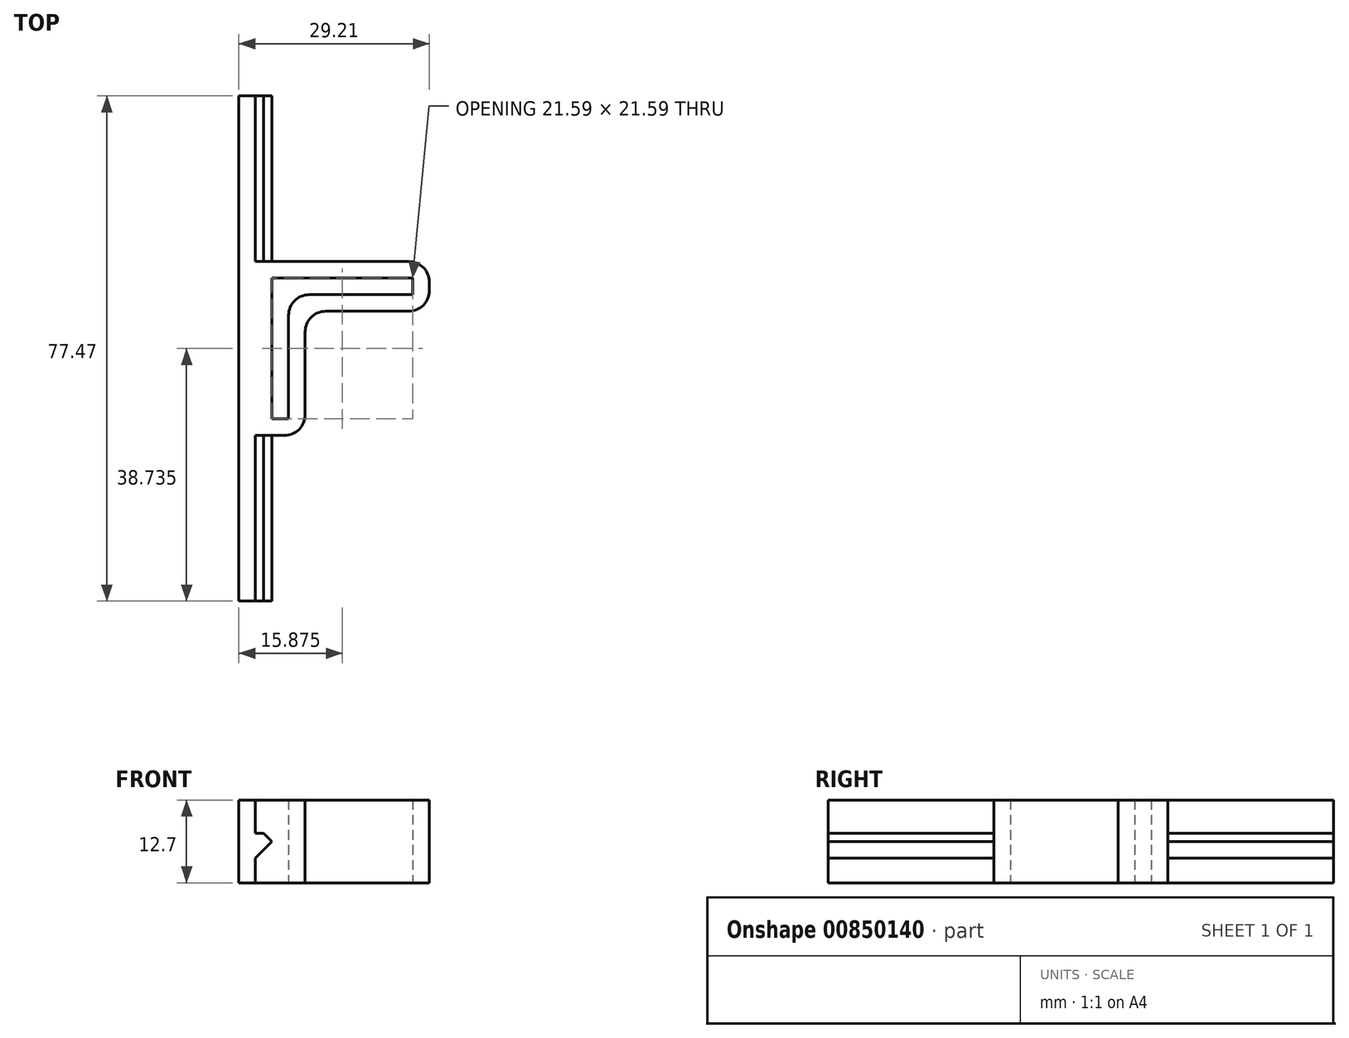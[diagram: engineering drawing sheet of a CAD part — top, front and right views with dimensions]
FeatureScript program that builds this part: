
annotation { "Feature Type Name" : "Feature", "Feature Type Description" : "" }
export const myFeature = defineFeature(function(context is Context, id is Id, definition is map)
    precondition{}
    {
        {
            var Q0;
            Q0=qCreatedBy(makeId("Top.planeOp"),FACE);
            var sketch = newSketch(context, id + "F0", { "sketchPlane" : qUnion([Q0])});
            skLineSegment(sketch, "E0.bottom", {"start": v(2.54, 0) * mm, "end": v(5.08, 0) * mm});
            skLineSegment(sketch, "E0.top", {"start": v(2.54, 21.6) * mm, "end": v(5.08, 21.6) * mm});
            skLineSegment(sketch, "E0.left", {"start": v(2.54, 0) * mm, "end": v(2.54, 21.59) * mm});
            skLineSegment(sketch, "E0.right", {"start": v(5.08, 0) * mm, "end": v(5.08, 19.05) * mm});
            skLineSegment(sketch, "E1.bottom", {"start": v(5.08, 21.6) * mm, "end": v(24.13, 21.6) * mm});
            skLineSegment(sketch, "E1.top", {"start": v(5.08, 19.05) * mm, "end": v(24.13, 19.05) * mm});
            skLineSegment(sketch, "E1.right", {"start": v(24.13, 21.6) * mm, "end": v(24.13, 19.05) * mm});
            skLineSegment(sketch, "E2", {"start": v(0, -2.2) * mm, "end": v(0, 24.13) * mm});
            skLineSegment(sketch, "E3", {"start": v(0, 24.13) * mm, "end": v(26.67, 24.13) * mm});
            skLineSegment(sketch, "E4", {"start": v(26.67, 24.13) * mm, "end": v(26.67, 16.51) * mm});
            skLineSegment(sketch, "E5", {"start": v(26.67, 16.51) * mm, "end": v(7.62, 16.5) * mm});
            skLineSegment(sketch, "E6", {"start": v(7.62, 16.5) * mm, "end": v(7.62, -2.54) * mm});
            skLineSegment(sketch, "E7", {"start": v(7.62, -2.54) * mm, "end": v(0, -2.54) * mm});
            skLineSegment(sketch, "E8", {"start": v(0, -2.54) * mm, "end": v(0, -2.2) * mm});
            skSolve(sketch);
        }
        {
            var Q0;
            Q0=qSketchRegion(id+"F0",true);
            extrude(context, id + "F1", {"entities" : qUnion([Q0]), "depth" : 12.7 * mm, "offsetDistance" : 25.4 * mm});
        }
        {
            var Q0;
            Q0=makeQuery(id+"F1.opExtrude","SWEPT_EDGE",EDGE,{"disambiguationData":[OSD([sQuery(id+"F0.wireOp",EDGE,"E3"),sQuery(id+"F0.wireOp",EDGE,"E4")])]});
            var Q1;
            Q1=makeQuery(id+"F1.opExtrude","SWEPT_EDGE",EDGE,{"disambiguationData":[OSD([sQuery(id+"F0.wireOp",EDGE,"E4"),sQuery(id+"F0.wireOp",EDGE,"E5")])]});
            var Q2;
            Q2=makeQuery(id+"F1.opExtrude","SWEPT_EDGE",EDGE,{"disambiguationData":[OSD([sQuery(id+"F0.wireOp",EDGE,"E0.right"),sQuery(id+"F0.wireOp",EDGE,"E1.top")])]});
            var Q3;
            Q3=makeQuery(id+"F1.opExtrude","SWEPT_EDGE",EDGE,{"disambiguationData":[OSD([sQuery(id+"F0.wireOp",EDGE,"E6"),sQuery(id+"F0.wireOp",EDGE,"E7")])]});
            var Q4;
            Q4=makeQuery(id+"F1.opExtrude","SWEPT_EDGE",EDGE,{"disambiguationData":[OSD([sQuery(id+"F0.wireOp",EDGE,"E5"),sQuery(id+"F0.wireOp",EDGE,"E6")])]});
            fillet(context, id + "F2", {"entities" : qUnion([Q0, Q1, Q2, Q3, Q4]), "radius" : 3.17 * mm, "tangentPropagation" : true, "allowEdgeOverflow" : false});
        }
        {
            var Q0;
            Q0=makeQuery(id+"F1.opExtrude","SWEPT_FACE",FACE,{"disambiguationData":[OSD([sQuery(id+"F0.wireOp",EDGE,"E2"),sQuery(id+"F0.wireOp",EDGE,"E8")])]});
            var sketch = newSketch(context, id + "F3", { "sketchPlane" : qUnion([Q0])});
            skLineSegment(sketch, "E9.bottom", {"start": v(-49.53, 12.7) * mm, "end": v(27.94, 12.7) * mm});
            skLineSegment(sketch, "E9.top", {"start": v(-49.53, 0) * mm, "end": v(27.94, 0) * mm});
            skLineSegment(sketch, "E9.left", {"start": v(-49.53, 12.7) * mm, "end": v(-49.53, 0) * mm});
            skLineSegment(sketch, "E9.right", {"start": v(27.94, 12.7) * mm, "end": v(27.94, 0) * mm});
            skSolve(sketch);
        }
        {
            var Q0;
            Q0 = qSketchRegion(id + "F3", true);
            extrude(context, id + "F4", {"entities" : qUnion([Q0]), "operationType" : NewBodyOperationType.ADD, "depth" : 2.54 * mm, "offsetDistance" : 25.4 * mm});
        }
        {
            var Q0;
            {var subQ0=sQuery(id+"F3.wireOp",EDGE,"E9.bottom");var subQ1=sQuery(id+"F0.wireOp",EDGE,"E3");var subQ2=sQuery(id+"F3.wireOp",EDGE,"E9.left");var subQ16=sQuery(id+"F3.wireOp",EDGE,"E9.top");Q0=makeQuery(id+"F4.boolean.opBoolean","SPLIT",FACE,{"disambiguationData":[TD([makeQuery(id+"F1.opExtrude","SWEPT_FACE",FACE,{"disambiguationData":[OSD([subQ1])]})])],"derivedFrom":makeQuery(id+"F4.opExtrude","CAP_FACE",FACE,{"disambiguationData":[OSD([subQ0,subQ16,subQ2,sQuery(id+"F3.wireOp",EDGE,"E9.right")])],"isStart":true})});}
            var sketch = newSketch(context, id + "F5", { "sketchPlane" : qUnion([Q0])});
            skLineSegment(sketch, "E10.bottom", {"start": v(24.13, 7.62) * mm, "end": v(49.53, 7.62) * mm});
            skLineSegment(sketch, "E10.top", {"start": v(24.13, 5.08) * mm, "end": v(49.53, 5.08) * mm});
            skLineSegment(sketch, "E10.left", {"start": v(24.13, 7.62) * mm, "end": v(24.13, 5.08) * mm});
            skLineSegment(sketch, "E10.right", {"start": v(49.53, 7.62) * mm, "end": v(49.53, 5.08) * mm});
            skLineSegment(sketch, "E11.bottom", {"start": v(-27.94, 5.08) * mm, "end": v(-2.54, 5.08) * mm});
            skLineSegment(sketch, "E11.top", {"start": v(-27.94, 7.62) * mm, "end": v(-2.54, 7.62) * mm});
            skLineSegment(sketch, "E11.left", {"start": v(-27.94, 5.08) * mm, "end": v(-27.94, 7.62) * mm});
            skLineSegment(sketch, "E11.right", {"start": v(-2.54, 5.08) * mm, "end": v(-2.54, 7.62) * mm});
            skSolve(sketch);
        }
        {
            var Q0;
            Q0 = qSketchRegion(id + "F5", true);
            extrude(context, id + "F6", {"entities" : qUnion([Q0]), "operationType" : NewBodyOperationType.ADD, "depth" : 2.54 * mm, "offsetDistance" : 25.4 * mm});
        }
        {
            var Q0;
            Q0=makeQuery(id+"F6.opExtrude","CAP_EDGE",EDGE,{"disambiguationData":[OSD([sQuery(id+"F5.wireOp",EDGE,"E11.bottom")])],"isStart":false});
            var Q1;
            Q1=makeQuery(id+"F6.opExtrude","CAP_EDGE",EDGE,{"disambiguationData":[OSD([sQuery(id+"F5.wireOp",EDGE,"E11.top")])],"isStart":false});
            var Q2;
            Q2=makeQuery(id+"F6.opExtrude","CAP_EDGE",EDGE,{"disambiguationData":[OSD([sQuery(id+"F5.wireOp",EDGE,"E10.bottom")])],"isStart":false});
            var Q3;
            Q3=makeQuery(id+"F6.opExtrude","CAP_EDGE",EDGE,{"disambiguationData":[OSD([sQuery(id+"F5.wireOp",EDGE,"E10.top")])],"isStart":false});
            var Q4;
            Q4=makeQuery(id+"F6.opExtrude","CAP_EDGE",EDGE,{"disambiguationData":[OSD([sQuery(id+"F5.wireOp",EDGE,"E11.bottom")])],"isStart":true});
            var Q5;
            Q5=makeQuery(id+"F6.opExtrude","CAP_EDGE",EDGE,{"disambiguationData":[OSD([sQuery(id+"F5.wireOp",EDGE,"E11.top")])],"isStart":true});
            var Q6;
            Q6=makeQuery(id+"F6.opExtrude","CAP_EDGE",EDGE,{"disambiguationData":[OSD([sQuery(id+"F5.wireOp",EDGE,"E10.bottom")])],"isStart":true});
            var Q7;
            Q7=makeQuery(id+"F6.opExtrude","CAP_EDGE",EDGE,{"disambiguationData":[OSD([sQuery(id+"F5.wireOp",EDGE,"E10.top")])],"isStart":true});
            chamfer(context, id + "F7", {"entities" : qUnion([Q0, Q1, Q2, Q3, Q4, Q5, Q6, Q7]), "width" : 1.27 * mm, "tangentPropagation" : true});
        }
    });
